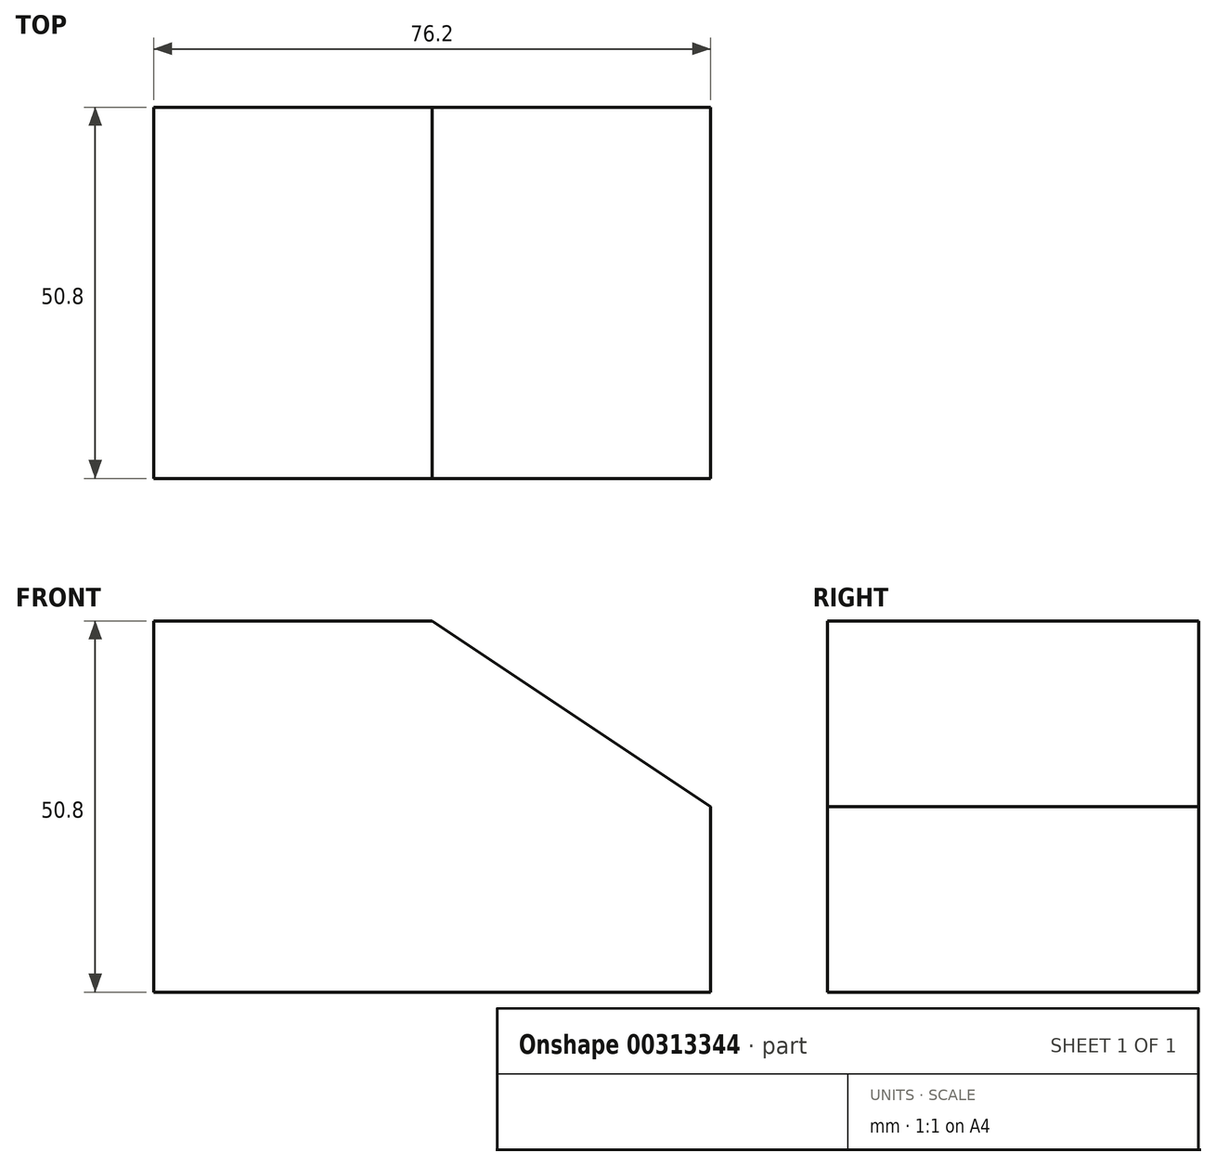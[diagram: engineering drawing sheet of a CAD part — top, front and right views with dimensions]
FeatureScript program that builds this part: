
annotation { "Feature Type Name" : "Feature", "Feature Type Description" : "" }
export const myFeature = defineFeature(function(context is Context, id is Id, definition is map)
    precondition{}
    {
        {
            var Q0;
            Q0=qCreatedBy(makeId("Front.planeOp"),FACE);
            var sketch = newSketch(context, id + "F0", { "sketchPlane" : qUnion([Q0])});
            skLineSegment(sketch, "E0", {"start": v(-54.79, -58.1) * mm, "end": v(21.41, -58.1) * mm});
            skLineSegment(sketch, "E1", {"start": v(-54.79, -58.1) * mm, "end": v(-54.79, -7.3) * mm});
            skLineSegment(sketch, "E2", {"start": v(-54.79, -7.3) * mm, "end": v(-16.69, -7.3) * mm});
            skLineSegment(sketch, "E3", {"start": v(21.41, -58.1) * mm, "end": v(21.41, -32.7) * mm});
            skLineSegment(sketch, "E4", {"start": v(21.41, -32.7) * mm, "end": v(-16.69, -7.3) * mm});
            skSolve(sketch);
        }
        {
            var Q0;
            Q0=makeQuery(id+"F0.imprint","IMPRINT",FACE,{"disambiguationData":[TD([[makeQuery(id+"F0.imprint","IMPRINT",EDGE,{"derivedFrom":sQuery(id+"F0.wireOp",EDGE,"E0")}),1.0]])]});
            extrude(context, id + "F1", {"entities" : qUnion([Q0]), "depth" : 50.8 * mm});
        }
    });
